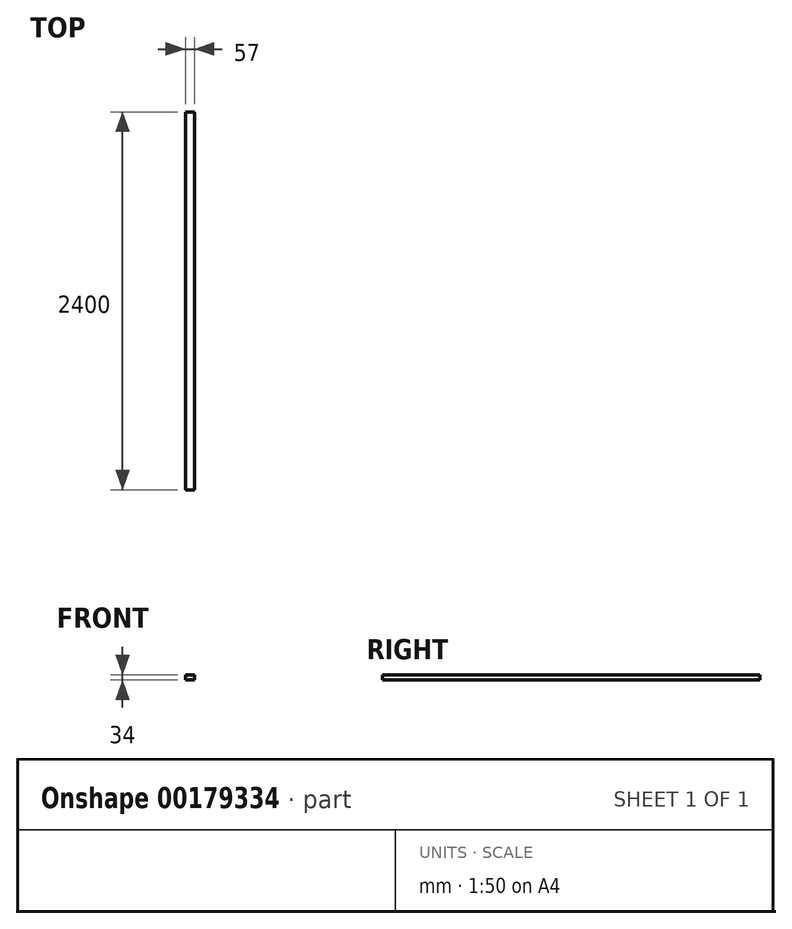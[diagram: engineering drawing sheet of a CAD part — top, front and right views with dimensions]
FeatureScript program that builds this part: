
annotation { "Feature Type Name" : "Feature", "Feature Type Description" : "" }
export const myFeature = defineFeature(function(context is Context, id is Id, definition is map)
    precondition{}
    {
        {
            var Q0;
            Q0=qCreatedBy(makeId("Front.planeOp"),FACE);
            var sketch = newSketch(context, id + "F0", { "sketchPlane" : qUnion([Q0])});
            skLineSegment(sketch, "E0.bottom", {"start": v(28.5, 17) * mm, "end": v(-28.5, 17) * mm});
            skLineSegment(sketch, "E0.top", {"start": v(28.5, -17) * mm, "end": v(-28.5, -17) * mm});
            skLineSegment(sketch, "E0.left", {"start": v(28.5, 17) * mm, "end": v(28.5, -17) * mm});
            skLineSegment(sketch, "E0.right", {"start": v(-28.5, 17) * mm, "end": v(-28.5, -17) * mm});
            skPoint(sketch, "E0.middle", {"position": v(0, 0) * mm});
            skSolve(sketch);
        }
        {
            var Q0;
            Q0=makeQuery(id+"F0.imprint","IMPRINT",FACE,{"disambiguationData":[TD([[makeQuery(id+"F0.imprint","IMPRINT",EDGE,{"derivedFrom":sQuery(id+"F0.wireOp",EDGE,"E0.bottom")}),1.0]])]});
            extrude(context, id + "F1", {"entities" : qUnion([Q0]), "depth" : 2400 * mm});
        }
    });
